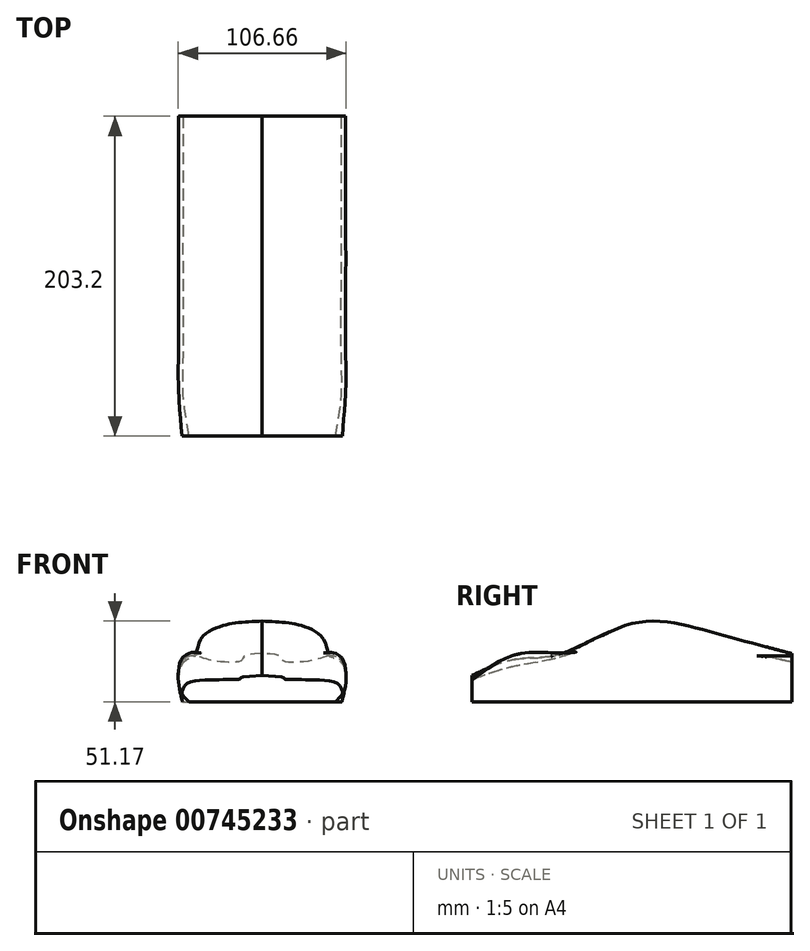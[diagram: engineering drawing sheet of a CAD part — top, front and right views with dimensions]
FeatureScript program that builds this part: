
annotation { "Feature Type Name" : "Feature", "Feature Type Description" : "" }
export const myFeature = defineFeature(function(context is Context, id is Id, definition is map)
    precondition{}
    {
        {
            var Q0;
            Q0=qCreatedBy(makeId("Front.planeOp"),FACE);
            var sketch = newSketch(context, id + "F0", { "sketchPlane" : qUnion([Q0])});
            skLineSegment(sketch, "E0", {"start": v(0, 0) * mm, "end": v(50.34, 0) * mm});
            skFitSpline(sketch, "E1", {"points": [v(50.34, 0) * mm, v(52.82, 11.05) * mm, v(50.34, 26.15) * mm, v(42.9, 29.09) * mm, v(34.8, 33.65) * mm, v(21.7, 40.86) * mm, v(0, 44.08) * mm], "startDerivative": vector(20.06, 64.7) * mm, "endDerivative": vector(-134.18, 5.53) * mm});
            skLineSegment(sketch, "E2", {"start": v(0, 44.08) * mm, "end": v(0, 0) * mm});
            skFitSpline(sketch, "E3.MirrorCS", {"points": [v(-50.34, 0) * mm, v(-52.82, 11.05) * mm, v(-50.34, 26.15) * mm, v(-42.9, 29.09) * mm, v(-34.8, 33.65) * mm, v(-21.7, 40.86) * mm, v(0, 44.08) * mm], "startDerivative": vector(-20.06, 64.7) * mm, "endDerivative": vector(134.18, 5.53) * mm});
            skLineSegment(sketch, "E4.MirrorCS", {"start": v(0, 0) * mm, "end": v(-50.34, 0) * mm});
            skSolve(sketch);
        }
        {
            var Q0;
            Q0=qCreatedBy(makeId("Front.planeOp"),FACE);
            cPlane(context, id + "F1", {"entities" : qUnion([Q0]), "cplaneType" : CPlaneType.OFFSET, "offset" : 50.8 * mm, "width" : 152.4 * mm, "height" : 152.4 * mm});
        }
        {
            var Q0;
            Q0=qCreatedBy(makeId("Front.planeOp"),FACE);
            cPlane(context, id + "F2", {"entities" : qUnion([Q0]), "cplaneType" : CPlaneType.OFFSET, "offset" : 101.6 * mm, "width" : 152.4 * mm, "height" : 152.4 * mm});
        }
        {
            var Q0;
            Q0=qCreatedBy(makeId("Front.planeOp"),FACE);
            cPlane(context, id + "F3", {"entities" : qUnion([Q0]), "cplaneType" : CPlaneType.OFFSET, "offset" : 50.8 * mm, "oppositeDirection" : true, "width" : 152.4 * mm, "height" : 152.4 * mm});
        }
        {
            var Q0;
            Q0=qCreatedBy(id+"F1.planeOp",FACE);
            var sketch = newSketch(context, id + "F4", { "sketchPlane" : qUnion([Q0])});
            skLineSegment(sketch, "E5", {"start": v(0, 0) * mm, "end": v(50.34, 0) * mm});
            skFitSpline(sketch, "E6", {"points": [v(50.34, 0) * mm, v(52.82, 11.05) * mm, v(50.34, 26.15) * mm, v(42.9, 29.09) * mm, v(38.61, 39.68) * mm, v(21.25, 48.02) * mm, v(0, 49.6) * mm], "startDerivative": vector(20.06, 64.7) * mm, "endDerivative": vector(-145.49, 5.54) * mm});
            skLineSegment(sketch, "E7", {"start": v(0, 49.6) * mm, "end": v(0, 0) * mm});
            skFitSpline(sketch, "E8.MirrorCS", {"points": [v(-50.34, 0) * mm, v(-52.82, 11.05) * mm, v(-50.34, 26.15) * mm, v(-42.9, 29.09) * mm, v(-38.61, 39.68) * mm, v(-21.25, 48.02) * mm, v(0, 49.6) * mm], "startDerivative": vector(-20.06, 64.7) * mm, "endDerivative": vector(145.49, 5.54) * mm});
            skLineSegment(sketch, "E9.MirrorCS", {"start": v(0, 0) * mm, "end": v(-50.34, 0) * mm});
            skSolve(sketch);
        }
        {
            var Q0;
            Q0=qCreatedBy(id+"F3.planeOp",FACE);
            var sketch = newSketch(context, id + "F5", { "sketchPlane" : qUnion([Q0])});
            skLineSegment(sketch, "E10", {"start": v(0, 0) * mm, "end": v(50.34, 0) * mm});
            skFitSpline(sketch, "E11", {"points": [v(50.34, 0) * mm, v(52.82, 11.05) * mm, v(50.34, 26.15) * mm, v(42.9, 29.09) * mm, v(33.03, 26.44) * mm, v(13.2, 25.99) * mm, v(0, 30.5) * mm], "startDerivative": vector(20.06, 64.7) * mm, "endDerivative": vector(-251.37, -3.52) * mm});
            skLineSegment(sketch, "E12", {"start": v(0, 30.5) * mm, "end": v(0, 0) * mm});
            skFitSpline(sketch, "E13.MirrorCS", {"points": [v(-50.34, 0) * mm, v(-52.82, 11.05) * mm, v(-50.34, 26.15) * mm, v(-42.9, 29.09) * mm, v(-33.03, 26.44) * mm, v(-13.2, 25.99) * mm, v(0, 30.5) * mm], "startDerivative": vector(-20.06, 64.7) * mm, "endDerivative": vector(251.37, -3.52) * mm});
            skLineSegment(sketch, "E14.MirrorCS", {"start": v(0, 0) * mm, "end": v(-50.34, 0) * mm});
            skSolve(sketch);
        }
        {
            var Q0;
            Q0=qCreatedBy(id+"F2.planeOp",FACE);
            var sketch = newSketch(context, id + "F6", { "sketchPlane" : qUnion([Q0])});
            skLineSegment(sketch, "E15", {"start": v(0, 0) * mm, "end": v(50.34, 0) * mm});
            skFitSpline(sketch, "E16", {"points": [v(50.34, 0) * mm, v(52.82, 11.05) * mm, v(50.34, 26.15) * mm, v(39.15, 31) * mm, v(31.57, 27.78) * mm, v(14.5, 28.16) * mm, v(0, 28.91) * mm], "startDerivative": vector(20.06, 64.7) * mm, "endDerivative": vector(-146.31, 0) * mm});
            skLineSegment(sketch, "E17", {"start": v(0, 28.91) * mm, "end": v(0, 0) * mm});
            skFitSpline(sketch, "E18.MirrorCS", {"points": [v(-50.34, 0) * mm, v(-52.82, 11.05) * mm, v(-50.34, 26.15) * mm, v(-39.15, 31) * mm, v(-31.57, 27.78) * mm, v(-14.5, 28.16) * mm, v(0, 28.91) * mm], "startDerivative": vector(-20.06, 64.7) * mm, "endDerivative": vector(146.31, 0) * mm});
            skLineSegment(sketch, "E19.MirrorCS", {"start": v(0, 0) * mm, "end": v(-50.34, 0) * mm});
            skSolve(sketch);
        }
        {
            var Q0;
            Q0=qCreatedBy(makeId("Front.planeOp"),FACE);
            cPlane(context, id + "F7", {"entities" : qUnion([Q0]), "cplaneType" : CPlaneType.OFFSET, "offset" : 127 * mm, "width" : 152.4 * mm, "height" : 152.4 * mm});
        }
        {
            var Q0;
            Q0=qCreatedBy(makeId("Front.planeOp"),FACE);
            cPlane(context, id + "F8", {"entities" : qUnion([Q0]), "cplaneType" : CPlaneType.OFFSET, "offset" : 152.4 * mm, "width" : 152.4 * mm, "height" : 152.4 * mm});
        }
        {
            var Q0;
            Q0=qCreatedBy(id+"F7.planeOp",FACE);
            var sketch = newSketch(context, id + "F9", { "sketchPlane" : qUnion([Q0])});
            skLineSegment(sketch, "E20", {"start": v(0, 0) * mm, "end": v(50.34, 0) * mm});
            skFitSpline(sketch, "E21", {"points": [v(50.34, 0) * mm, v(52.82, 11.05) * mm, v(50.34, 26.15) * mm, v(42.9, 29.09) * mm, v(33.5, 25.17) * mm, v(15.92, 22.62) * mm, v(0, 26.6) * mm], "startDerivative": vector(20.06, 64.7) * mm, "endDerivative": vector(-284.63, 0) * mm});
            skLineSegment(sketch, "E22", {"start": v(0, 26.6) * mm, "end": v(0, 0) * mm});
            skFitSpline(sketch, "E23.MirrorCS", {"points": [v(-50.34, 0) * mm, v(-52.82, 11.05) * mm, v(-50.34, 26.15) * mm, v(-42.9, 29.09) * mm, v(-33.5, 25.17) * mm, v(-15.92, 22.62) * mm, v(0, 26.6) * mm], "startDerivative": vector(-20.06, 64.7) * mm, "endDerivative": vector(284.63, 0) * mm});
            skLineSegment(sketch, "E24.MirrorCS", {"start": v(0, 0) * mm, "end": v(-50.34, 0) * mm});
            skSolve(sketch);
        }
        {
            var Q0;
            Q0=qCreatedBy(id+"F8.planeOp",FACE);
            var sketch = newSketch(context, id + "F10", { "sketchPlane" : qUnion([Q0])});
            skLineSegment(sketch, "E25", {"start": v(0, 0) * mm, "end": v(46.55, 0) * mm});
            skFitSpline(sketch, "E26", {"points": [v(46.55, 0) * mm, v(50.72, 7.3) * mm, v(46.55, 12.23) * mm, v(33.08, 13.75) * mm, v(22.28, 14.12) * mm, v(14.5, 14.31) * mm, v(0, 16.59) * mm], "startDerivative": vector(94.6, 83.18) * mm, "endDerivative": vector(-247.18, 8.47) * mm});
            skLineSegment(sketch, "E27", {"start": v(0, 16.59) * mm, "end": v(0, 0) * mm});
            skFitSpline(sketch, "E28.MirrorCS", {"points": [v(-46.55, 0) * mm, v(-50.72, 7.3) * mm, v(-46.55, 12.23) * mm, v(-33.08, 13.75) * mm, v(-22.28, 14.12) * mm, v(-14.5, 14.31) * mm, v(0, 16.59) * mm], "startDerivative": vector(-94.6, 83.18) * mm, "endDerivative": vector(247.18, 8.47) * mm});
            skLineSegment(sketch, "E29.MirrorCS", {"start": v(0, 0) * mm, "end": v(-46.55, 0) * mm});
            skSolve(sketch);
        }
        {
            var Q0;
            Q0=makeQuery(id+"F10.imprint","IMPRINT",FACE,{"disambiguationData":[TD([[makeQuery(id+"F10.imprint","IMPRINT",EDGE,{"derivedFrom":sQuery(id+"F10.wireOp",EDGE,"E25")}),1.0]])]});
            var Q1;
            Q1=makeQuery(id+"F9.imprint","IMPRINT",FACE,{"disambiguationData":[TD([[makeQuery(id+"F9.imprint","IMPRINT",EDGE,{"derivedFrom":sQuery(id+"F9.wireOp",EDGE,"E20")}),1.0]])]});
            var Q2;
            Q2=makeQuery(id+"F6.imprint","IMPRINT",FACE,{"disambiguationData":[TD([[makeQuery(id+"F6.imprint","IMPRINT",EDGE,{"derivedFrom":sQuery(id+"F6.wireOp",EDGE,"E15")}),1.0]])]});
            var Q3;
            Q3=makeQuery(id+"F4.imprint","IMPRINT",FACE,{"disambiguationData":[TD([[makeQuery(id+"F4.imprint","IMPRINT",EDGE,{"derivedFrom":sQuery(id+"F4.wireOp",EDGE,"E5")}),1.0]])]});
            var Q4;
            Q4=makeQuery(id+"F0.imprint","IMPRINT",FACE,{"disambiguationData":[TD([[makeQuery(id+"F0.imprint","IMPRINT",EDGE,{"derivedFrom":sQuery(id+"F0.wireOp",EDGE,"E0")}),1.0]])]});
            var Q5;
            Q5=makeQuery(id+"F5.imprint","IMPRINT",FACE,{"disambiguationData":[TD([[makeQuery(id+"F5.imprint","IMPRINT",EDGE,{"derivedFrom":sQuery(id+"F5.wireOp",EDGE,"E10")}),1.0]])]});
            loft(context, id + "F11", {"sheetProfilesArray" : [{ "sheetProfileEntities" : qUnion([Q0]) }, { "sheetProfileEntities" : qUnion([Q1]) }, { "sheetProfileEntities" : qUnion([Q2]) }, { "sheetProfileEntities" : qUnion([Q3]) }, { "sheetProfileEntities" : qUnion([Q4]) }, { "sheetProfileEntities" : qUnion([Q5]) }]});
        }
        {
            var Q0;
            Q0=makeQuery(id+"F11.opLoft","SWEPT_BODY",BODY,{"disambiguationData":[OSD([sQuery(id+"F0.wireOp",EDGE,"E2"),sQuery(id+"F4.wireOp",EDGE,"E7"),makeQuery(id+"F5.imprint","IMPRINT",FACE,{"disambiguationData":[TD([[makeQuery(id+"F5.imprint","IMPRINT",EDGE,{"derivedFrom":sQuery(id+"F5.wireOp",EDGE,"E10")}),1.0]])]}),sQuery(id+"F6.wireOp",EDGE,"E17"),sQuery(id+"F9.wireOp",EDGE,"E22"),makeQuery(id+"F10.imprint","IMPRINT",FACE,{"disambiguationData":[TD([[makeQuery(id+"F10.imprint","IMPRINT",EDGE,{"derivedFrom":sQuery(id+"F10.wireOp",EDGE,"E25")}),1.0]])]})])]});
            var Q1;
            Q1=qCreatedBy(makeId("Right.planeOp"),FACE);
            mirror(context, id + "F12", {"operationType" : NewBodyOperationType.ADD, "entities" : qUnion([Q0]), "mirrorPlane" : qUnion([Q1])});
        }
    });
